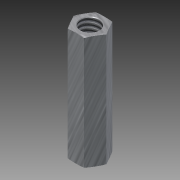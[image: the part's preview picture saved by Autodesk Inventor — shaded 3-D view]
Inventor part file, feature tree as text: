
AUTODESK INVENTOR PART (.ipt)
format: ipt  version: 2011 (Build 150239000, 239)  size: 119,296 bytes
history: native  units: in
note: dims shown in document units (in); Inventor stores cm internally (conversion verified against a paired STEP export)
features: other x1, imported_body x1, thread x1
ambient origin geometry x8: Origin, YZ Plane, XZ Plane, XY Plane, X Axis, Y Axis, Z Axis, Center Point
feature tree (3):
  parser-record x1  (decoder bookkeeping rows leaked as tree rows — omitted from the tree; the rows remain in map.json)
  imported_body  "Base1"
  thread  "Thread1"  [1 undecoded]
note: 1 required parameter value undecoded (feature->parameter linkage not recoverable at this tier; creation-order binding heuristic only, values carry confidence <= 0.55)
